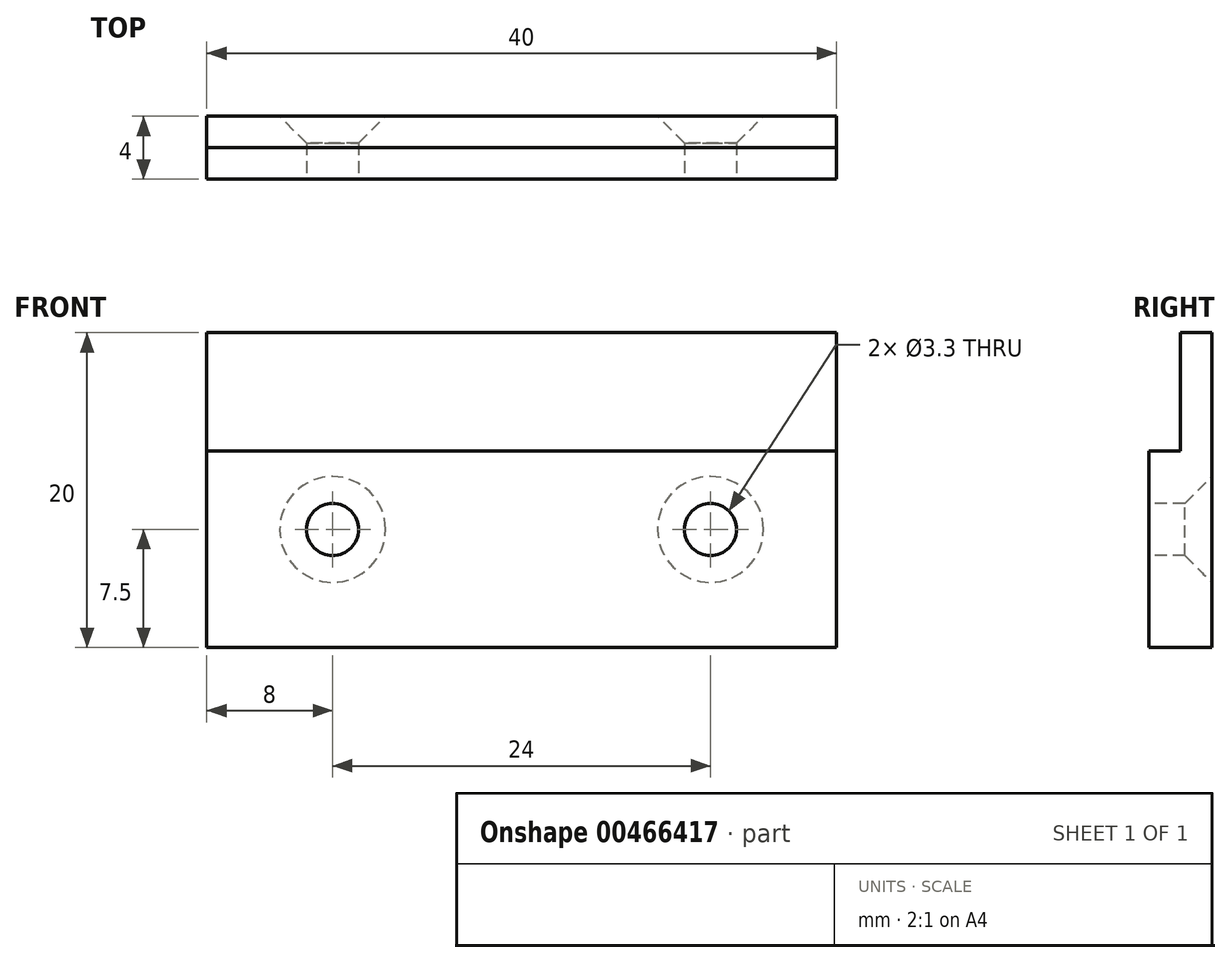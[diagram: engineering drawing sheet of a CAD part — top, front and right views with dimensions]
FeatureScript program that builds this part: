
annotation { "Feature Type Name" : "Feature", "Feature Type Description" : "" }
export const myFeature = defineFeature(function(context is Context, id is Id, definition is map)
    precondition{}
    {
        {
            var Q0;
            Q0=qCreatedBy(makeId("Front.planeOp"),FACE);
            var sketch = newSketch(context, id + "F0", { "sketchPlane" : qUnion([Q0])});
            skLineSegment(sketch, "E0.bottom", {"start": v(20, -10) * mm, "end": v(-20, -10) * mm});
            skLineSegment(sketch, "E0.top", {"start": v(20, 10) * mm, "end": v(-20, 10) * mm});
            skLineSegment(sketch, "E0.left", {"start": v(20, -10) * mm, "end": v(20, 10) * mm});
            skLineSegment(sketch, "E0.right", {"start": v(-20, -10) * mm, "end": v(-20, 10) * mm});
            skPoint(sketch, "E0.middle", {"position": v(0, 0) * mm});
            skPoint(sketch, "E1.startSnap0", {"position": v(-20, 0) * mm});
            skLineSegment(sketch, "E2", {"start": v(-20, 2.5) * mm, "end": v(20, 2.5) * mm});
            skPoint(sketch, "E3", {"position": v(-12, -2.5) * mm});
            skPoint(sketch, "E4", {"position": v(12, -2.5) * mm});
            skLineSegment(sketch, "E5", {"start": v(-20, -2.5) * mm, "end": v(20, -2.5) * mm, "construction": true});
            skSolve(sketch);
        }
        {
            var Q0;
            {var subQ0=sQuery(id+"F0.wireOp",EDGE,"E0.top");Q0=makeQuery(id+"F0.imprint","IMPRINT",FACE,{"disambiguationData":[TD([[makeQuery(id+"F0.imprint","IMPRINT",EDGE,{"derivedFrom":subQ0}),1.0]])]});}
            extrude(context, id + "F1", {"entities" : qUnion([Q0]), "depth" : 2 * mm, "offsetDistance" : 25 * mm});
        }
        {
            var Q0;
            {var subQ0=sQuery(id+"F0.wireOp",EDGE,"E0.bottom");Q0=makeQuery(id+"F0.imprint","IMPRINT",FACE,{"disambiguationData":[TD([[makeQuery(id+"F0.imprint","IMPRINT",EDGE,{"derivedFrom":subQ0}),-1.0]])]});}
            extrude(context, id + "F2", {"entities" : qUnion([Q0]), "operationType" : NewBodyOperationType.ADD, "depth" : 4 * mm, "offsetDistance" : 25 * mm});
        }
        {
            var Q0;
            Q0=sQuery(id+"F0.wireOp",VERTEX,"E3");
            var Q1;
            Q1=sQuery(id+"F0.wireOp",VERTEX,"E4");
            var Q2;
            Q2=makeQuery(id+"F1.opExtrude","SWEPT_BODY",BODY,{"disambiguationData":[OSD([sQuery(id+"F0.wireOp",EDGE,"E0.top"),sQuery(id+"F0.wireOp",EDGE,"E0.left"),sQuery(id+"F0.wireOp",EDGE,"E0.right"),sQuery(id+"F0.wireOp",EDGE,"E2")])]});
            hole(context, id + "F3", {"style" : HoleStyle.C_SINK, "endStyle" : HoleEndStyle.THROUGH, "oppositeDirection" : true, "standardTappedOrClearance" : lookupTablePath({ "standard" : "ISO", "fit" : "Normal", "size" : "M3", "type" : "Clearance" }), "standardBlindInLast" : lookupTablePath({ "fit" : "Standard", "standard" : "ISO", "size" : "M3", "type" : "Clearance" }), "holeDiameter" : 3.3 * mm, "cSinkDiameter" : 6.72 * mm, "cSinkAngle" : 90 * degree, "majorDiameter" : 5 * mm, "isTappedThrough" : true, "tappedDepth" : 12 * mm, "tapClearance" : 3, "locations" : qUnion([Q0, Q1]), "scope" : qUnion([Q2]), "startStyle" : HoleStartStyle.PART});
        }
    });
